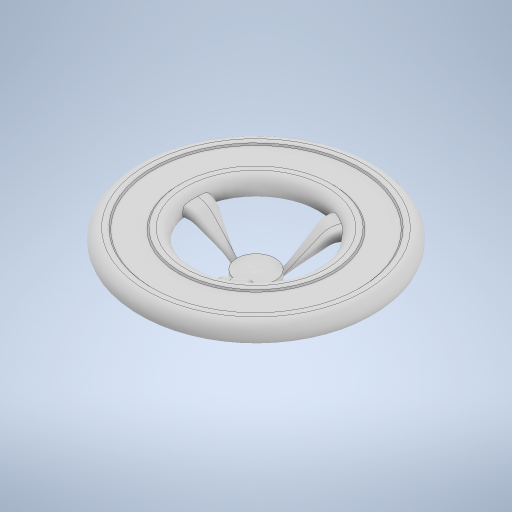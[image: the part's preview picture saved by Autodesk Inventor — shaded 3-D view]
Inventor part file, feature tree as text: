
AUTODESK INVENTOR PART (.ipt)
format: ipt  version: 2023 (Build 270158000, 158)  size: 539,136 bytes
history: native  units: mm
features: sketch x4, other x2, revolve x1, loft x1, pattern_circular x1
ambient origin geometry x8: Origin, YZ Plane, XZ Plane, XY Plane, X Axis, Y Axis, Z Axis, Center Point
bodies: Solido1 (feature_tree)
feature tree (9):
  revolve  "Rivoluzione1"
  sketch  "Schizzo2"
  sketch  "Schizzo3"
  sketch  "Schizzo 3D2"
  loft  "Loft1"
  pattern_circular  "Serie circolare1"  [2 undecoded]
  sketch  "Schizzo1"
  other  "Proietta su superficie1"
  other  "Proietta su superficie2"
note: 2 required parameter values undecoded (feature->parameter linkage not recoverable at this tier; creation-order binding heuristic only, values carry confidence <= 0.55)
